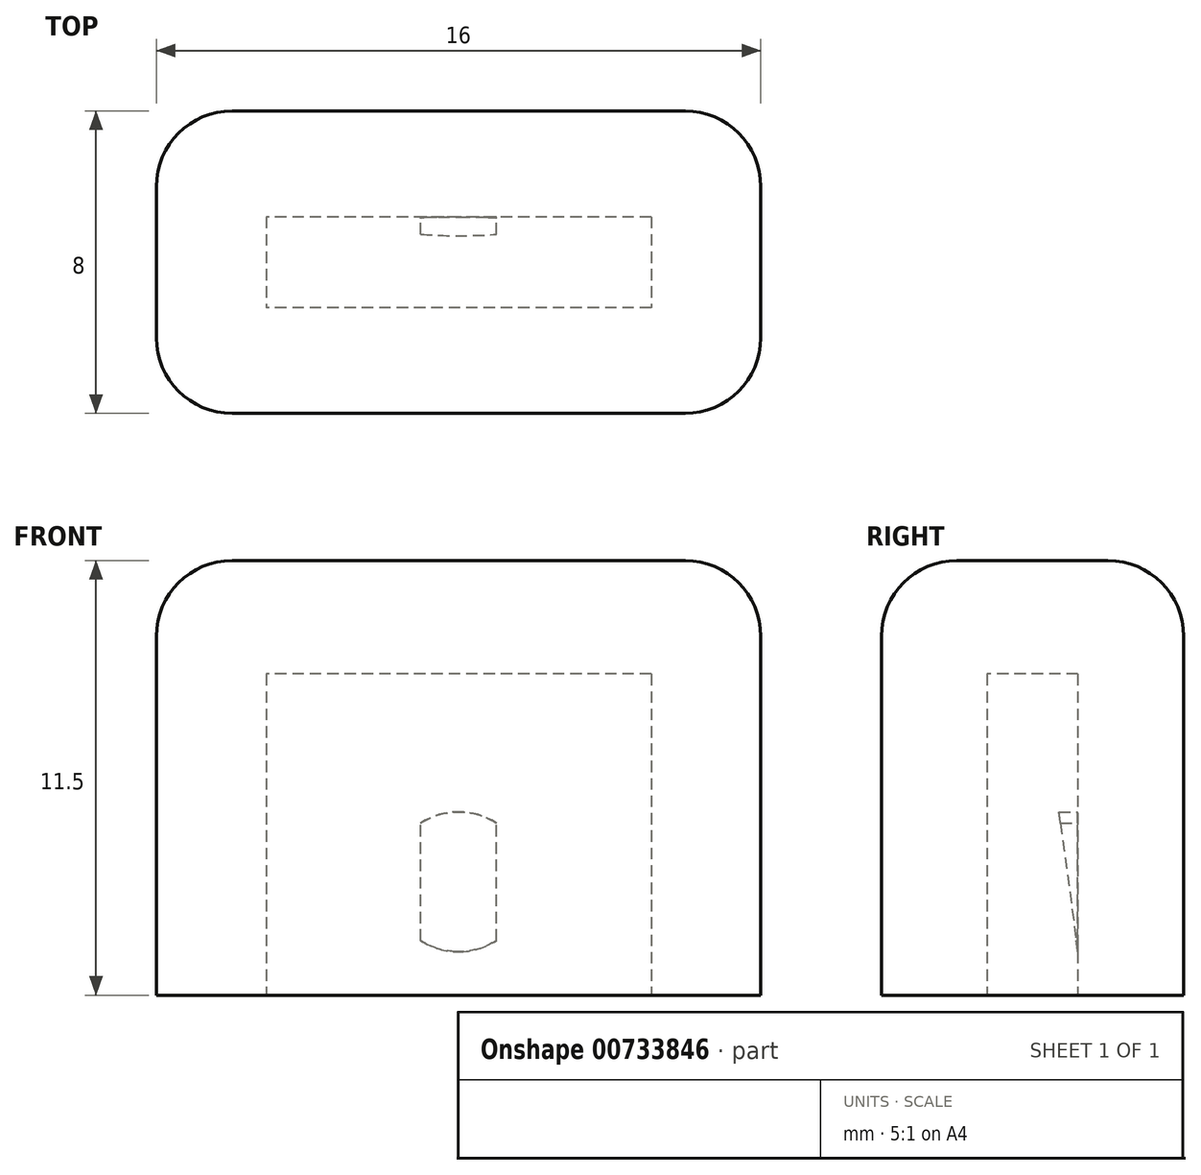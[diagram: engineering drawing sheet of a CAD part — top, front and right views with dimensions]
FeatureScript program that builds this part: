
annotation { "Feature Type Name" : "Feature", "Feature Type Description" : "" }
export const myFeature = defineFeature(function(context is Context, id is Id, definition is map)
    precondition{}
    {
        {
            var Q0;
            Q0=qCreatedBy(makeId("Top.planeOp"),FACE);
            var sketch = newSketch(context, id + "F0", { "sketchPlane" : qUnion([Q0])});
            skLineSegment(sketch, "E0.bottom", {"start": v(8, -4) * mm, "end": v(-8, -4) * mm});
            skLineSegment(sketch, "E0.top", {"start": v(8, 4) * mm, "end": v(-8, 4) * mm});
            skLineSegment(sketch, "E0.left", {"start": v(8, -4) * mm, "end": v(8, 4) * mm});
            skLineSegment(sketch, "E0.right", {"start": v(-8, -4) * mm, "end": v(-8, 4) * mm});
            skPoint(sketch, "E0.middle", {"position": v(0, 0) * mm});
            skSolve(sketch);
        }
        {
            var Q0;
            Q0 = qSketchRegion(id + "F0", true);
            extrude(context, id + "F1", {"entities" : qUnion([Q0]), "depth" : 11.5 * mm, "offsetDistance" : 25 * mm});
        }
        {
            var Q0;
            Q0=makeQuery(id+"F1.opExtrude","CAP_FACE",FACE,{"disambiguationData":[OSD([sQuery(id+"F0.wireOp",EDGE,"E0.bottom"),sQuery(id+"F0.wireOp",EDGE,"E0.top"),sQuery(id+"F0.wireOp",EDGE,"E0.left"),sQuery(id+"F0.wireOp",EDGE,"E0.right")])],"isStart":true});
            var sketch = newSketch(context, id + "F2", { "sketchPlane" : qUnion([Q0])});
            skLineSegment(sketch, "E1.bottom", {"start": v(5.1, -1.2) * mm, "end": v(-5.1, -1.2) * mm});
            skLineSegment(sketch, "E1.top", {"start": v(5.1, 1.2) * mm, "end": v(-5.1, 1.2) * mm});
            skLineSegment(sketch, "E1.left", {"start": v(5.1, -1.2) * mm, "end": v(5.1, 1.2) * mm});
            skLineSegment(sketch, "E1.right", {"start": v(-5.1, -1.2) * mm, "end": v(-5.1, 1.2) * mm});
            skPoint(sketch, "E1.middle", {"position": v(0, 0) * mm});
            skSolve(sketch);
        }
        {
            var Q0;
            Q0 = qSketchRegion(id + "F2", true);
            extrude(context, id + "F3", {"entities" : qUnion([Q0]), "operationType" : NewBodyOperationType.REMOVE, "oppositeDirection" : true, "depth" : 8.5 * mm, "offsetDistance" : 25 * mm});
        }
        {
            var Q0;
            Q0=makeQuery(id+"F3.boolean.opBoolean","COPY",FACE,{"derivedFrom":makeQuery(id+"F3.opExtrude","SWEPT_FACE",FACE,{"disambiguationData":[OSD([sQuery(id+"F2.wireOp",EDGE,"E1.bottom")])]})});
            var sketch = newSketch(context, id + "F4", { "sketchPlane" : qUnion([Q0])});
            skCircle(sketch, "E2", {"center": v(0, 3) * mm, "radius": 1.85 * mm});
            skPoint(sketch, "E2.centerSnap0", {"position": v(0, 0) * mm});
            skSolve(sketch);
        }
        {
            var Q0;
            Q0 = qSketchRegion(id + "F4", true);
            extrude(context, id + "F5", {"entities" : qUnion([Q0]), "depth" : .5 * mm, "offsetDistance" : 25 * mm});
        }
        {
            var Q0;
            Q0=makeQuery(id+"F3.boolean.opBoolean","COPY",FACE,{"derivedFrom":makeQuery(id+"F3.opExtrude","SWEPT_FACE",FACE,{"disambiguationData":[OSD([sQuery(id+"F2.wireOp",EDGE,"E1.bottom")])]})});
            var sketch = newSketch(context, id + "F6", { "sketchPlane" : qUnion([Q0])});
            skLineSegment(sketch, "E3.bottom", {"start": v(2.54, 5.7) * mm, "end": v(-2.54, 5.7) * mm});
            skLineSegment(sketch, "E3.top", {"start": v(2.54, 1.22) * mm, "end": v(-2.54, 1.22) * mm});
            skLineSegment(sketch, "E3.left", {"start": v(2.54, 5.7) * mm, "end": v(2.54, 1.22) * mm});
            skLineSegment(sketch, "E3.right", {"start": v(-2.54, 5.7) * mm, "end": v(-2.54, 1.22) * mm});
            skPoint(sketch, "E3.middle", {"position": v(0, 3.46) * mm});
            skPoint(sketch, "E3.middle.positionSnap0", {"position": v(0, 0) * mm});
            skPoint(sketch, "E3.centerSnap0", {"position": v(0, 0) * mm});
            skSolve(sketch);
        }
        {
            var Q0;
            Q0=makeQuery(id+"F6.imprint","IMPRINT",FACE,{"disambiguationData":[TD([[makeQuery(id+"F6.imprint","IMPRINT",EDGE,{"derivedFrom":sQuery(id+"F6.wireOp",EDGE,"E3.bottom")}),-1.0]])]});
            var sketch = newSketch(context, id + "F7", { "sketchPlane" : qUnion([Q0])});
            skLineSegment(sketch, "E4.bottom", {"start": v(1, 1.15) * mm, "end": v(-1, 1.15) * mm});
            skLineSegment(sketch, "E4.top", {"start": v(1, 4.85) * mm, "end": v(-1, 4.85) * mm});
            skLineSegment(sketch, "E4.left", {"start": v(1, 1.15) * mm, "end": v(1, 4.85) * mm});
            skLineSegment(sketch, "E4.right", {"start": v(-1, 1.15) * mm, "end": v(-1, 4.85) * mm});
            skPoint(sketch, "E4.middle", {"position": v(0, 3) * mm});
            skSolve(sketch);
        }
        {
            var Q0;
            Q0 = qSketchRegion(id + "F7", true);
            extrude(context, id + "F8", {"entities" : qUnion([Q0]), "depth" : 0.8 * mm, "offsetDistance" : 25 * mm});
        }
        {
            var Q0;
            Q0=makeQuery(id+"F8.opExtrude","CAP_EDGE",EDGE,{"disambiguationData":[OSD([sQuery(id+"F7.wireOp",EDGE,"E4.bottom")])],"isStart":false});
            chamfer(context, id + "F9", {"entities" : qUnion([Q0]), "chamferType" : ChamferType.TWO_OFFSETS, "width1" : 0.5 * mm, "oppositeDirection" : false, "width2" : 3.7 * mm, "tangentPropagation" : true});
        }
        {
            var Q0;
            Q0=makeQuery(id+"F8.opExtrude","SWEPT_BODY",BODY,{"disambiguationData":[OSD([sQuery(id+"F7.wireOp",EDGE,"E4.bottom"),sQuery(id+"F7.wireOp",EDGE,"E4.top"),sQuery(id+"F7.wireOp",EDGE,"E4.left"),sQuery(id+"F7.wireOp",EDGE,"E4.right")])]});
            deleteBodies(context, id + "F10", {"entities" : qUnion([Q0])});
        }
        {
            var Q0;
            Q0=qCreatedBy(makeId("Right.planeOp"),FACE);
            var sketch = newSketch(context, id + "F11", { "sketchPlane" : qUnion([Q0])});
            skLineSegment(sketch, "E5", {"start": v(1.2, 4.85) * mm, "end": v(0.7, 4.85) * mm});
            skLineSegment(sketch, "E6", {"start": v(0.7, 4.85) * mm, "end": v(1.2, 1.15) * mm});
            skLineSegment(sketch, "E7", {"start": v(1.2, 1.15) * mm, "end": v(1.2, 4.85) * mm});
            skSolve(sketch);
        }
        {
            var Q0;
            Q0 = qSketchRegion(id + "F11", true);
            extrude(context, id + "F12", {"entities" : qUnion([Q0]), "endBound" : BoundingType.SYMMETRIC, "depth" : 2 * mm, "offsetDistance" : 25 * mm});
        }
        {
            var Q0;
            Q0=makeQuery(id+"F5.opExtrude","SWEPT_BODY",BODY,{"disambiguationData":[OSD([sQuery(id+"F4.wireOp",EDGE,"E2")])]});
            var Q1;
            Q1=makeQuery(id+"F12.opExtrude","SWEPT_BODY",BODY,{"disambiguationData":[OSD([sQuery(id+"F11.wireOp",EDGE,"E5"),sQuery(id+"F11.wireOp",EDGE,"E6"),sQuery(id+"F11.wireOp",EDGE,"E7")])]});
            booleanBodies(context, id + "F13", {"operationType" : BooleanOperationType.INTERSECTION, "tools" : qUnion([Q0, Q1])});
        }
        {
            var Q0;
            Q0=makeQuery(id+"F1.opExtrude","CAP_EDGE",EDGE,{"disambiguationData":[OSD([sQuery(id+"F0.wireOp",EDGE,"E0.bottom")])],"isStart":false});
            var Q1;
            Q1=makeQuery(id+"F1.opExtrude","CAP_EDGE",EDGE,{"disambiguationData":[OSD([sQuery(id+"F0.wireOp",EDGE,"E0.top")])],"isStart":false});
            var Q2;
            Q2=makeQuery(id+"F1.opExtrude","CAP_EDGE",EDGE,{"disambiguationData":[OSD([sQuery(id+"F0.wireOp",EDGE,"E0.left")])],"isStart":false});
            var Q3;
            Q3=makeQuery(id+"F1.opExtrude","CAP_EDGE",EDGE,{"disambiguationData":[OSD([sQuery(id+"F0.wireOp",EDGE,"E0.right")])],"isStart":false});
            var Q4;
            Q4=makeQuery(id+"F1.opExtrude","SWEPT_EDGE",EDGE,{"disambiguationData":[OSD([sQuery(id+"F0.wireOp",EDGE,"E0.bottom"),sQuery(id+"F0.wireOp",EDGE,"E0.right")])]});
            var Q5;
            Q5=makeQuery(id+"F1.opExtrude","SWEPT_EDGE",EDGE,{"disambiguationData":[OSD([sQuery(id+"F0.wireOp",EDGE,"E0.bottom"),sQuery(id+"F0.wireOp",EDGE,"E0.left")])]});
            var Q6;
            Q6=makeQuery(id+"F1.opExtrude","SWEPT_EDGE",EDGE,{"disambiguationData":[OSD([sQuery(id+"F0.wireOp",EDGE,"E0.top"),sQuery(id+"F0.wireOp",EDGE,"E0.left")])]});
            var Q7;
            Q7=makeQuery(id+"F1.opExtrude","SWEPT_EDGE",EDGE,{"disambiguationData":[OSD([sQuery(id+"F0.wireOp",EDGE,"E0.top"),sQuery(id+"F0.wireOp",EDGE,"E0.right")])]});
            fillet(context, id + "F14", {"entities" : qUnion([Q0, Q1, Q2, Q3, Q4, Q5, Q6, Q7]), "radius" : 2 * mm, "tangentPropagation" : true, "allowEdgeOverflow" : false});
        }
    });
